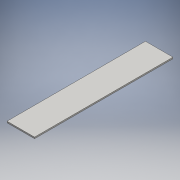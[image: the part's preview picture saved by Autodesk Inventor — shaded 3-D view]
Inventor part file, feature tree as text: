
AUTODESK INVENTOR PART (.ipt)
format: ipt  version: 2016 SP1 (Build 200210100, 210)  size: 88,576 bytes
history: native  units: mm
features: extrude x1, sketch x1
ambient origin geometry x8: Origin, YZ Plane, XZ Plane, XY Plane, X Axis, Y Axis, Z Axis, Center Point
bodies: Solid1 (feature_tree)
feature tree (2):
  extrude  "Extrusion1"  Depth=287.0mm
  sketch  "Sketch1"  dims[d0=57.0mm d1=287.0mm d2=143.5mm d3=28.5mm d4=3.0mm d5=0.0mm]
